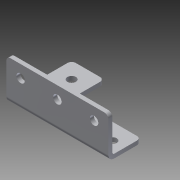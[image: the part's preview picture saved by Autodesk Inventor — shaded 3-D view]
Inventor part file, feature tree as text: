
AUTODESK INVENTOR PART (.ipt)
format: ipt  version: 2013 (Build 170138000, 138)  size: 217,088 bytes
history: native  units: in
note: dims shown in document units (in); Inventor stores cm internally (conversion verified against a paired STEP export)
features: sheet_metal_op x4, other x4, sketch x3, chamfer x1
ambient origin geometry x8: Origin, YZ Plane, XZ Plane, XY Plane, X Axis, Y Axis, Z Axis, Center Point
feature tree (12):
  sheet_metal_op  "Face1"
  sheet_metal_op  "Flange1"
  chamfer  "Corner Round1"
  sketch  "Sketch1"  dims[d0=2.0in]
  other  "Plate1"
  sketch  "Sketch2"  dims[d1=1.0in]
  other  "Plate2"
  sheet_metal_op  "Bend1"
  sheet_metal_op  "Corner1"
  sketch  "Sketch3"  dims[d2=0.26in d3=0.26in d4=1.0in d8=0.125in d9=0.125in d10=0.0625in d11=0.25in d12=0.125in d13=1.25in d14=90.0deg d15=0.05in d16=0.5in d17=0.125in d18=0.125in d19=0.26in d22=0.125in d23=0.0in d24=0.125in d25=2.125in d26=2.25in d27=0.75in d28=0.875in d29=2.25in d5=0.125in d6=0.0in d7=0.25in]
  other  "Cut1"
  other  "Definition1"
